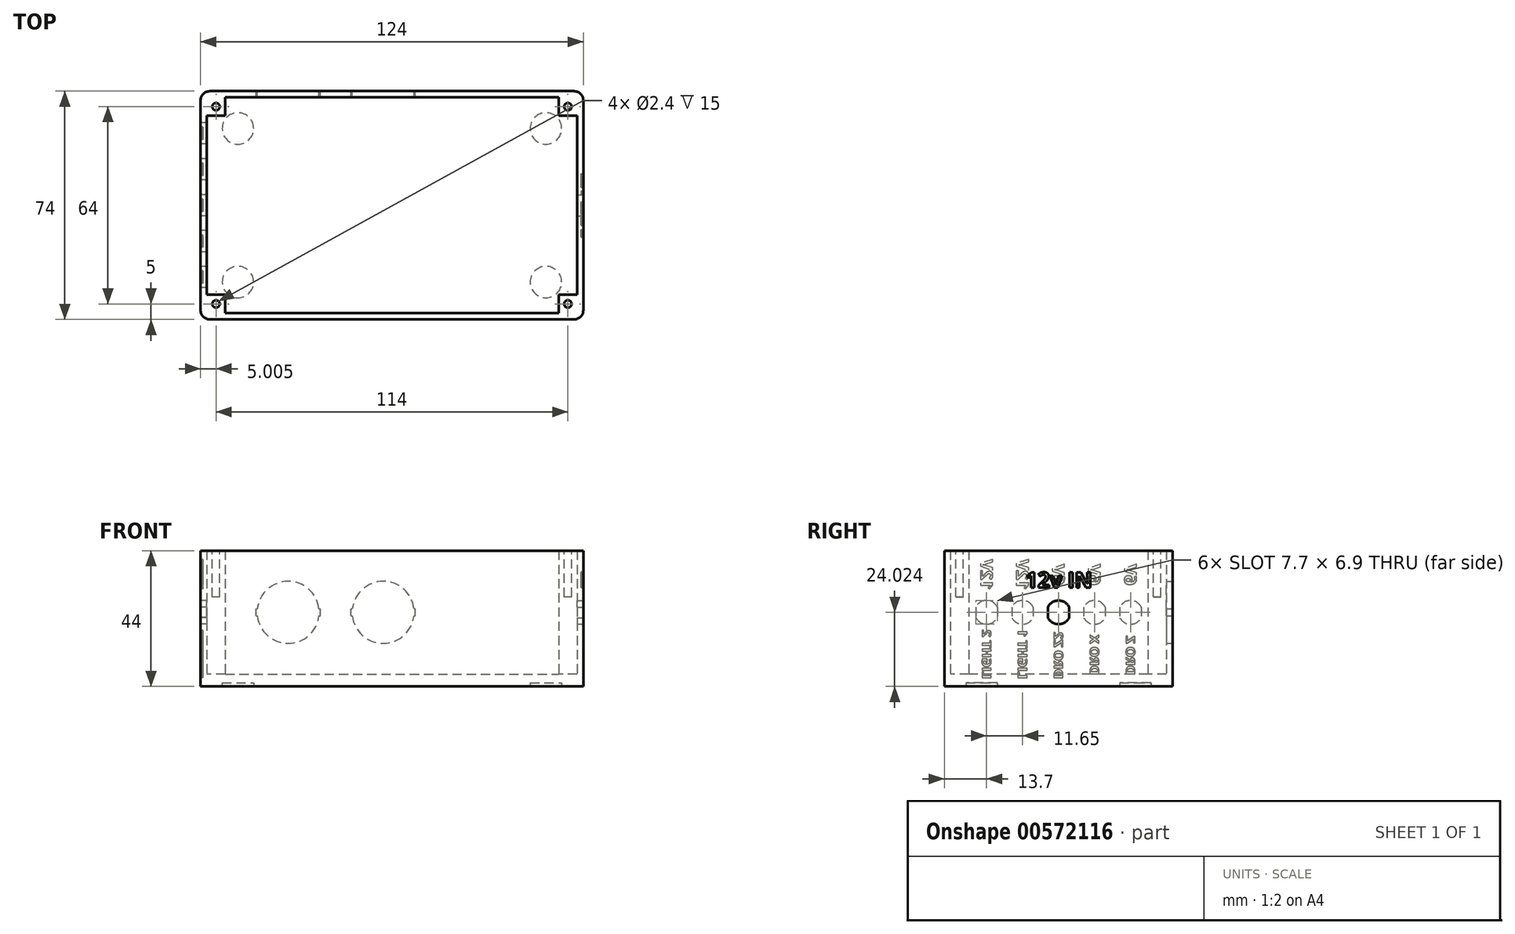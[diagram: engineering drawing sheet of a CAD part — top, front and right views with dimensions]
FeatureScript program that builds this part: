
annotation { "Feature Type Name" : "Feature", "Feature Type Description" : "" }
export const myFeature = defineFeature(function(context is Context, id is Id, definition is map)
    precondition{}
    {
        {
            var Q0;
            Q0=qCreatedBy(makeId("Top.planeOp"),FACE);
            var sketch = newSketch(context, id + "F0", { "sketchPlane" : qUnion([Q0])});
            skLineSegment(sketch, "E0.bottom", {"start": v(-65.67, 30.67) * mm, "end": v(58.33, 30.67) * mm});
            skLineSegment(sketch, "E0.top", {"start": v(-65.67, -43.33) * mm, "end": v(58.33, -43.33) * mm});
            skLineSegment(sketch, "E0.left", {"start": v(-65.67, 30.67) * mm, "end": v(-65.67, -43.33) * mm});
            skLineSegment(sketch, "E0.right", {"start": v(58.33, 30.67) * mm, "end": v(58.33, -43.33) * mm});
            skSolve(sketch);
        }
        {
            var Q0;
            Q0=makeQuery(id+"F0.imprint","IMPRINT",FACE,{"disambiguationData":[TD([[makeQuery(id+"F0.imprint","IMPRINT",EDGE,{"derivedFrom":sQuery(id+"F0.wireOp",EDGE,"E0.bottom")}),-1.0]])]});
            extrude(context, id + "F1", {"entities" : qUnion([Q0]), "depth" : 44 * mm, "offsetDistance" : 25 * mm});
        }
        {
            var Q0;
            Q0=makeQuery(id+"F1.opExtrude","CAP_FACE",FACE,{"disambiguationData":[OSD([sQuery(id+"F0.wireOp",EDGE,"E0.bottom"),sQuery(id+"F0.wireOp",EDGE,"E0.top"),sQuery(id+"F0.wireOp",EDGE,"E0.left"),sQuery(id+"F0.wireOp",EDGE,"E0.right")])],"isStart":false});
            var sketch = newSketch(context, id + "F2", { "sketchPlane" : qUnion([Q0])});
            skLineSegment(sketch, "E1.bottom", {"start": v(-63.67, 28.67) * mm, "end": v(56.33, 28.67) * mm});
            skLineSegment(sketch, "E1.top", {"start": v(-63.67, -41.33) * mm, "end": v(56.33, -41.33) * mm});
            skLineSegment(sketch, "E1.left", {"start": v(-63.67, 28.67) * mm, "end": v(-63.67, -41.33) * mm});
            skLineSegment(sketch, "E1.right", {"start": v(56.33, 28.67) * mm, "end": v(56.33, -41.33) * mm});
            skSolve(sketch);
        }
        {
            var Q0;
            Q0 = qSketchRegion(id + "F2", true);
            extrude(context, id + "F3", {"entities" : qUnion([Q0]), "operationType" : NewBodyOperationType.REMOVE, "oppositeDirection" : true, "depth" : 40 * mm, "offsetDistance" : 25 * mm});
        }
        {
            var Q0;
            Q0=makeQuery(id+"F3.boolean.opBoolean","COPY",FACE,{"derivedFrom":makeQuery(id+"F3.opExtrude","CAP_FACE",FACE,{"disambiguationData":[OSD([sQuery(id+"F2.wireOp",EDGE,"E1.bottom"),sQuery(id+"F2.wireOp",EDGE,"E1.top"),sQuery(id+"F2.wireOp",EDGE,"E1.left"),sQuery(id+"F2.wireOp",EDGE,"E1.right")])],"isStart":false})});
            var sketch = newSketch(context, id + "F4", { "sketchPlane" : qUnion([Q0])});
            skLineSegment(sketch, "E2.bottom", {"start": v(-57.67, 28.67) * mm, "end": v(-63.67, 28.67) * mm});
            skLineSegment(sketch, "E2.top", {"start": v(-57.67, 22.67) * mm, "end": v(-63.67, 22.67) * mm});
            skLineSegment(sketch, "E2.left", {"start": v(-57.67, 28.67) * mm, "end": v(-57.67, 22.67) * mm});
            skLineSegment(sketch, "E2.right", {"start": v(-63.67, 28.67) * mm, "end": v(-63.67, 22.67) * mm});
            skLineSegment(sketch, "E3.bottom", {"start": v(-63.67, -35.33) * mm, "end": v(-57.67, -35.33) * mm});
            skLineSegment(sketch, "E3.top", {"start": v(-63.67, -41.33) * mm, "end": v(-57.67, -41.33) * mm});
            skLineSegment(sketch, "E3.left", {"start": v(-63.67, -35.33) * mm, "end": v(-63.67, -41.33) * mm});
            skLineSegment(sketch, "E3.right", {"start": v(-57.67, -35.33) * mm, "end": v(-57.67, -41.33) * mm});
            skLineSegment(sketch, "E4.bottom", {"start": v(50.33, 28.67) * mm, "end": v(56.33, 28.67) * mm});
            skLineSegment(sketch, "E4.top", {"start": v(50.33, 22.67) * mm, "end": v(56.33, 22.67) * mm});
            skLineSegment(sketch, "E4.left", {"start": v(50.33, 28.67) * mm, "end": v(50.33, 22.67) * mm});
            skLineSegment(sketch, "E4.right", {"start": v(56.33, 28.67) * mm, "end": v(56.33, 22.67) * mm});
            skLineSegment(sketch, "E5.bottom", {"start": v(56.33, -35.33) * mm, "end": v(50.33, -35.33) * mm});
            skLineSegment(sketch, "E5.top", {"start": v(56.33, -41.33) * mm, "end": v(50.33, -41.33) * mm});
            skLineSegment(sketch, "E5.left", {"start": v(56.33, -35.33) * mm, "end": v(56.33, -41.33) * mm});
            skLineSegment(sketch, "E5.right", {"start": v(50.33, -35.33) * mm, "end": v(50.33, -41.33) * mm});
            skSolve(sketch);
        }
        {
            var Q0;
            Q0=makeQuery(id+"F4.imprint","IMPRINT",FACE,{"disambiguationData":[TD([[makeQuery(id+"F4.imprint","IMPRINT",EDGE,{"derivedFrom":sQuery(id+"F4.wireOp",EDGE,"E2.bottom")}),-1.0]])]});
            var Q1;
            Q1=makeQuery(id+"F4.imprint","IMPRINT",FACE,{"disambiguationData":[TD([[makeQuery(id+"F4.imprint","IMPRINT",EDGE,{"derivedFrom":sQuery(id+"F4.wireOp",EDGE,"E3.bottom")}),-1.0]])]});
            var Q2;
            Q2=makeQuery(id+"F4.imprint","IMPRINT",FACE,{"disambiguationData":[TD([[makeQuery(id+"F4.imprint","IMPRINT",EDGE,{"derivedFrom":sQuery(id+"F4.wireOp",EDGE,"E5.bottom")}),1.0]])]});
            var Q3;
            Q3=makeQuery(id+"F4.imprint","IMPRINT",FACE,{"disambiguationData":[TD([[makeQuery(id+"F4.imprint","IMPRINT",EDGE,{"derivedFrom":sQuery(id+"F4.wireOp",EDGE,"E4.bottom")}),-1.0]])]});
            extrude(context, id + "F5", {"entities" : qUnion([Q0, Q1, Q2, Q3]), "operationType" : NewBodyOperationType.ADD, "depth" : 40 * mm, "offsetDistance" : 25 * mm});
        }
        {
            var Q0;
            Q0=makeQuery(id+"F1.opExtrude","SWEPT_FACE",FACE,{"disambiguationData":[OSD([sQuery(id+"F0.wireOp",EDGE,"E0.right")])]});
            var sketch = newSketch(context, id + "F6", { "sketchPlane" : qUnion([Q0])});
            skPoint(sketch, "E6.centerSnap0", {"position": v(-43.33, 22) * mm});
            skPoint(sketch, "E6.centerSnap1", {"position": v(-6.33, 44) * mm});
            skText(sketch, "E7", { "text": "12v IN", "fontName": "OpenSans-Bold.ttf"});
            skLineSegment(sketch, "E8", {"start": v(-6.33, 44) * mm, "end": v(-6.33, 0) * mm, "construction": true});
            skLineSegment(sketch, "E9", {"start": v(-46.35, 24) * mm, "end": v(35.36, 24) * mm, "construction": true});
            skLineSegment(sketch, "E10", {"start": v(-47, 4) * mm, "end": v(35.52, 4) * mm, "construction": true});
            const initialGuessF6  = {"E7": [-0.01706, 0.03203, 1, 0, 0.005]};
            skSetInitialGuess(sketch, initialGuessF6);
            skSolve(sketch);
        }
        {
            var Q0;
            Q0 = qSketchRegion(id + "F6", true);
            extrude(context, id + "F7", {"entities" : qUnion([Q0]), "operationType" : NewBodyOperationType.REMOVE, "oppositeDirection" : true, "depth" : 0.7 * mm, "offsetDistance" : 25 * mm});
        }
        {
            var Q0;
            Q0=makeQuery(id+"F6.imprint","IMPRINT",FACE,{"disambiguationData":[TD([[makeQuery(id+"F6.imprint","IMPRINT",EDGE,{"derivedFrom":sQuery(id+"F6.wireOp",EDGE,"E7.sketch_text.stroke-0")}),1.0]])]});
            var sketch = newSketch(context, id + "F8", { "sketchPlane" : qUnion([Q0])});
            skLineSegment(sketch, "E11", {"start": v(33.2, 0) * mm, "end": v(-45.85, 0) * mm, "construction": true});
            skLineSegment(sketch, "E12", {"start": v(-45.85, 4) * mm, "end": v(34.48, 4) * mm, "construction": true});
            skLineSegment(sketch, "E13", {"start": v(34.48, 24) * mm, "end": v(-45.85, 24) * mm, "construction": true});
            skLineSegment(sketch, "E14", {"start": v(30.67, 0) * mm, "end": v(30.67, 44.64) * mm, "construction": true});
            skLineSegment(sketch, "E15", {"start": v(-43.33, 0) * mm, "end": v(-43.33, 45.27) * mm, "construction": true});
            skLineSegment(sketch, "E16", {"start": v(-6.33, -5.83) * mm, "end": v(-6.33, 47.57) * mm, "construction": true});
            skPoint(sketch, "E16.startSnap0", {"position": v(-6.33, 0) * mm});
            skArc(sketch, "E17", {"start": v(-9.78, 22.3) * mm, "mid": v(-6.33, 20.15) * mm, "end": v(-2.88, 22.3) * mm});
            skLineSegment(sketch, "E18", {"start": v(-2.88, 25.7) * mm, "end": v(-2.88, 22.3) * mm});
            skLineSegment(sketch, "E19", {"start": v(-9.78, 25.7) * mm, "end": v(-9.78, 22.3) * mm});
            skArc(sketch, "E20.trimOffspring", {"start": v(-2.88, 25.7) * mm, "mid": v(-6.33, 27.85) * mm, "end": v(-9.78, 25.7) * mm});
            skSolve(sketch);
        }
        {
            var Q0;
            Q0=makeQuery(id+"F1.opExtrude","CAP_FACE",FACE,{"disambiguationData":[OSD([sQuery(id+"F0.wireOp",EDGE,"E0.bottom"),sQuery(id+"F0.wireOp",EDGE,"E0.top"),sQuery(id+"F0.wireOp",EDGE,"E0.left"),sQuery(id+"F0.wireOp",EDGE,"E0.right")])],"isStart":true});
            var sketch = newSketch(context, id + "F9", { "sketchPlane" : qUnion([Q0])});
            skCircle(sketch, "E21", {"center": v(46.23, 31.23) * mm, "radius": 5.1 * mm});
            skCircle(sketch, "E22", {"center": v(46.23, -18.57) * mm, "radius": 5.1 * mm});
            skCircle(sketch, "E23", {"center": v(-53.57, 31.23) * mm, "radius": 5.1 * mm});
            skCircle(sketch, "E24", {"center": v(-53.57, -18.57) * mm, "radius": 5.1 * mm});
            skSolve(sketch);
        }
        {
            var Q0;
            Q0=makeQuery(id+"F9.imprint","IMPRINT",FACE,{"disambiguationData":[TD([[makeQuery(id+"F9.imprint","IMPRINT",EDGE,{"derivedFrom":sQuery(id+"F9.wireOp",EDGE,"E23")}),1.0]])]});
            var Q1;
            Q1=makeQuery(id+"F9.imprint","IMPRINT",FACE,{"disambiguationData":[TD([[makeQuery(id+"F9.imprint","IMPRINT",EDGE,{"derivedFrom":sQuery(id+"F9.wireOp",EDGE,"E24")}),1.0]])]});
            var Q2;
            Q2=makeQuery(id+"F9.imprint","IMPRINT",FACE,{"disambiguationData":[TD([[makeQuery(id+"F9.imprint","IMPRINT",EDGE,{"derivedFrom":sQuery(id+"F9.wireOp",EDGE,"E22")}),1.0]])]});
            var Q3;
            Q3=makeQuery(id+"F9.imprint","IMPRINT",FACE,{"disambiguationData":[TD([[makeQuery(id+"F9.imprint","IMPRINT",EDGE,{"derivedFrom":sQuery(id+"F9.wireOp",EDGE,"E21")}),1.0]])]});
            extrude(context, id + "F10", {"entities" : qUnion([Q0, Q1, Q2, Q3]), "operationType" : NewBodyOperationType.REMOVE, "oppositeDirection" : true, "depth" : 1.1 * mm, "offsetDistance" : 25 * mm});
        }
        {
            var Q0;
            Q0=makeQuery(id+"F5.boolean.opBoolean","MERGE",FACE,{"derivedFrom":[makeQuery(id+"F1.opExtrude","CAP_FACE",FACE,{"disambiguationData":[OSD([sQuery(id+"F0.wireOp",EDGE,"E0.bottom"),sQuery(id+"F0.wireOp",EDGE,"E0.top"),sQuery(id+"F0.wireOp",EDGE,"E0.left"),sQuery(id+"F0.wireOp",EDGE,"E0.right")])],"isStart":false}),makeQuery(id+"F5.opExtrude","CAP_FACE",FACE,{"disambiguationData":[OSD([sQuery(id+"F4.wireOp",EDGE,"E2.bottom"),sQuery(id+"F4.wireOp",EDGE,"E2.top"),sQuery(id+"F4.wireOp",EDGE,"E2.left"),sQuery(id+"F4.wireOp",EDGE,"E2.right")])],"isStart":false}),makeQuery(id+"F5.opExtrude","CAP_FACE",FACE,{"disambiguationData":[OSD([sQuery(id+"F4.wireOp",EDGE,"E3.bottom"),sQuery(id+"F4.wireOp",EDGE,"E3.top"),sQuery(id+"F4.wireOp",EDGE,"E3.left"),sQuery(id+"F4.wireOp",EDGE,"E3.right")])],"isStart":false}),makeQuery(id+"F5.opExtrude","CAP_FACE",FACE,{"disambiguationData":[OSD([sQuery(id+"F4.wireOp",EDGE,"E4.bottom"),sQuery(id+"F4.wireOp",EDGE,"E4.top"),sQuery(id+"F4.wireOp",EDGE,"E4.left"),sQuery(id+"F4.wireOp",EDGE,"E4.right")])],"isStart":false}),makeQuery(id+"F5.opExtrude","CAP_FACE",FACE,{"disambiguationData":[OSD([sQuery(id+"F4.wireOp",EDGE,"E5.bottom"),sQuery(id+"F4.wireOp",EDGE,"E5.top"),sQuery(id+"F4.wireOp",EDGE,"E5.left"),sQuery(id+"F4.wireOp",EDGE,"E5.right")])],"isStart":false})]});
            var sketch = newSketch(context, id + "F11", { "sketchPlane" : qUnion([Q0])});
            skCircle(sketch, "E25", {"center": v(-60.67, 25.67) * mm, "radius": 1.2 * mm});
            skPoint(sketch, "E25.centerSnap0", {"position": v(-60.67, 22.67) * mm});
            skPoint(sketch, "E25.centerSnap1", {"position": v(-57.67, 25.67) * mm});
            skCircle(sketch, "E26", {"center": v(-60.67, -38.33) * mm, "radius": 1.2 * mm});
            skPoint(sketch, "E26.centerSnap0", {"position": v(-60.67, -35.33) * mm});
            skPoint(sketch, "E26.centerSnap1", {"position": v(-57.67, -38.33) * mm});
            skCircle(sketch, "E27", {"center": v(53.33, 25.67) * mm, "radius": 1.2 * mm});
            skPoint(sketch, "E27.centerSnap0", {"position": v(50.33, 25.67) * mm});
            skPoint(sketch, "E27.centerSnap1", {"position": v(53.33, 22.67) * mm});
            skCircle(sketch, "E28", {"center": v(53.33, -38.33) * mm, "radius": 1.2 * mm});
            skPoint(sketch, "E28.centerSnap0", {"position": v(50.33, -38.33) * mm});
            skPoint(sketch, "E28.centerSnap1", {"position": v(53.33, -35.33) * mm});
            skSolve(sketch);
        }
        {
            var Q0;
            Q0=makeQuery(id+"F11.imprint","IMPRINT",FACE,{"disambiguationData":[TD([[makeQuery(id+"F11.imprint","IMPRINT",EDGE,{"derivedFrom":sQuery(id+"F11.wireOp",EDGE,"E26")}),1.0]])]});
            var Q1;
            Q1=makeQuery(id+"F11.imprint","IMPRINT",FACE,{"disambiguationData":[TD([[makeQuery(id+"F11.imprint","IMPRINT",EDGE,{"derivedFrom":sQuery(id+"F11.wireOp",EDGE,"E27")}),1.0]])]});
            var Q2;
            Q2=makeQuery(id+"F11.imprint","IMPRINT",FACE,{"disambiguationData":[TD([[makeQuery(id+"F11.imprint","IMPRINT",EDGE,{"derivedFrom":sQuery(id+"F11.wireOp",EDGE,"E28")}),1.0]])]});
            var Q3;
            Q3=makeQuery(id+"F11.imprint","IMPRINT",FACE,{"disambiguationData":[TD([[makeQuery(id+"F11.imprint","IMPRINT",EDGE,{"derivedFrom":sQuery(id+"F11.wireOp",EDGE,"E25")}),1.0]])]});
            extrude(context, id + "F12", {"entities" : qUnion([Q0, Q1, Q2, Q3]), "operationType" : NewBodyOperationType.REMOVE, "oppositeDirection" : true, "depth" : 15 * mm, "offsetDistance" : 25 * mm});
        }
        {
            var Q0;
            Q0=makeQuery(id+"F1.opExtrude","SWEPT_FACE",FACE,{"disambiguationData":[OSD([sQuery(id+"F0.wireOp",EDGE,"E0.bottom")])]});
            var sketch = newSketch(context, id + "F13", { "sketchPlane" : qUnion([Q0])});
            skArc(sketch, "E29", {"start": v(27.3, 22.85) * mm, "mid": v(37.28, 13.95) * mm, "end": v(47.26, 22.85) * mm});
            skLineSegment(sketch, "E30.bottom", {"start": v(47.67, 22.85) * mm, "end": v(47.26, 22.85) * mm});
            skLineSegment(sketch, "E30.top", {"start": v(47.67, 25.15) * mm, "end": v(47.26, 25.15) * mm});
            skLineSegment(sketch, "E30.left", {"start": v(47.67, 22.85) * mm, "end": v(47.67, 25.15) * mm});
            skLineSegment(sketch, "E30.right", {"start": v(26.9, 22.85) * mm, "end": v(26.9, 25.15) * mm});
            skLineSegment(sketch, "E31.trimOffspring", {"start": v(27.3, 22.85) * mm, "end": v(26.9, 22.85) * mm});
            skArc(sketch, "E32.trimOffspring", {"start": v(47.26, 25.15) * mm, "mid": v(37.28, 34.05) * mm, "end": v(27.3, 25.15) * mm});
            skLineSegment(sketch, "E33.trimOffspring", {"start": v(27.3, 25.15) * mm, "end": v(26.9, 25.15) * mm});
            skLineSegment(sketch, "E34", {"start": v(37.28, 24) * mm, "end": v(-29.07, 24) * mm, "construction": true});
            skLineSegment(sketch, "E35", {"start": v(37.28, 24) * mm, "end": v(65.67, 24) * mm, "construction": true});
            skLineSegment(sketch, "E36", {"start": v(57.67, 44) * mm, "end": v(57.67, 0) * mm, "construction": true});
            skLineSegment(sketch, "E37", {"start": v(1.3, 4) * mm, "end": v(75.25, 4) * mm, "construction": true});
            skArc(sketch, "E38", {"start": v(-3.48, 22.85) * mm, "mid": v(6.5, 13.95) * mm, "end": v(16.49, 22.85) * mm});
            skLineSegment(sketch, "E39.bottom", {"start": v(16.9, 22.85) * mm, "end": v(16.49, 22.85) * mm});
            skLineSegment(sketch, "E39.top", {"start": v(16.9, 25.15) * mm, "end": v(16.49, 25.15) * mm});
            skLineSegment(sketch, "E39.left", {"start": v(16.9, 22.85) * mm, "end": v(16.9, 25.15) * mm});
            skLineSegment(sketch, "E39.right", {"start": v(-3.88, 22.85) * mm, "end": v(-3.88, 25.15) * mm});
            skLineSegment(sketch, "E40.trimOffspring", {"start": v(-3.48, 22.85) * mm, "end": v(-3.88, 22.85) * mm});
            skArc(sketch, "E41.trimOffspring", {"start": v(16.49, 25.15) * mm, "mid": v(6.5, 34.05) * mm, "end": v(-3.48, 25.15) * mm});
            skLineSegment(sketch, "E42.trimOffspring", {"start": v(-3.48, 25.15) * mm, "end": v(-3.88, 25.15) * mm});
            skSolve(sketch);
        }
        {
            var Q0;
            Q0=makeQuery(id+"F13.imprint","IMPRINT",FACE,{"disambiguationData":[TD([[makeQuery(id+"F13.imprint","IMPRINT",EDGE,{"derivedFrom":sQuery(id+"F13.wireOp",EDGE,"E29")}),1.0]])]});
            var Q1;
            Q1=makeQuery(id+"F13.imprint","IMPRINT",FACE,{"disambiguationData":[TD([[makeQuery(id+"F13.imprint","IMPRINT",EDGE,{"derivedFrom":sQuery(id+"F13.wireOp",EDGE,"E38")}),1.0]])]});
            extrude(context, id + "F14", {"entities" : qUnion([Q0, Q1]), "operationType" : NewBodyOperationType.REMOVE, "endBound" : BoundingType.UP_TO_NEXT, "oppositeDirection" : true, "depth" : 3 * mm, "offsetDistance" : 25 * mm});
        }
        {
            var Q0;
            Q0=makeQuery(id+"F1.opExtrude","SWEPT_FACE",FACE,{"disambiguationData":[OSD([sQuery(id+"F0.wireOp",EDGE,"E0.left")])]});
            var sketch = newSketch(context, id + "F15", { "sketchPlane" : qUnion([Q0])});
            skLineSegment(sketch, "E43", {"start": v(-47.32, 4) * mm, "end": v(59.37, 4) * mm, "construction": true});
            skLineSegment(sketch, "E44", {"start": v(-24.67, 44) * mm, "end": v(-24.67, 0) * mm, "construction": true});
            skLineSegment(sketch, "E45", {"start": v(37.33, 44) * mm, "end": v(37.33, 0) * mm, "construction": true});
            skPoint(sketch, "E46.startSnap0", {"position": v(6.33, 44) * mm});
            skPoint(sketch, "E46.endSnap0", {"position": v(6.33, 0) * mm});
            skArc(sketch, "E47", {"start": v(2.88, 22.3) * mm, "mid": v(6.33, 20.15) * mm, "end": v(9.78, 22.3) * mm});
            skArc(sketch, "E48", {"start": v(26.18, 22.32) * mm, "mid": v(29.63, 20.17) * mm, "end": v(33.08, 22.32) * mm});
            skLineSegment(sketch, "E49", {"start": v(6.33, 44) * mm, "end": v(6.33, 0) * mm, "construction": true});
            skArc(sketch, "E50", {"start": v(14.53, 22.3) * mm, "mid": v(17.98, 20.15) * mm, "end": v(21.43, 22.3) * mm});
            skArc(sketch, "E51", {"start": v(-8.77, 22.3) * mm, "mid": v(-5.32, 20.15) * mm, "end": v(-1.87, 22.3) * mm});
            skArc(sketch, "E52", {"start": v(-13.55, 25.7) * mm, "mid": v(-17, 27.85) * mm, "end": v(-20.45, 25.7) * mm});
            skPoint(sketch, "E53", {"position": v(23.15, 24) * mm});
            skLineSegment(sketch, "E54", {"start": v(-33.7, 24) * mm, "end": v(49.69, 24) * mm, "construction": true});
            skLineSegment(sketch, "E55", {"start": v(33.48, 35.36) * mm, "end": v(33.48, 8.32) * mm, "construction": true});
            skLineSegment(sketch, "E56", {"start": v(-13.55, 25.7) * mm, "end": v(-13.55, 22.3) * mm});
            skLineSegment(sketch, "E57", {"start": v(-20.45, 25.7) * mm, "end": v(-20.45, 22.3) * mm});
            skLineSegment(sketch, "E58", {"start": v(-8.77, 25.7) * mm, "end": v(-8.77, 22.3) * mm});
            skLineSegment(sketch, "E59", {"start": v(-1.87, 25.7) * mm, "end": v(-1.87, 22.3) * mm});
            skLineSegment(sketch, "E60", {"start": v(2.88, 25.7) * mm, "end": v(2.88, 22.3) * mm});
            skLineSegment(sketch, "E61", {"start": v(9.78, 25.7) * mm, "end": v(9.78, 22.3) * mm});
            skLineSegment(sketch, "E62", {"start": v(14.53, 25.7) * mm, "end": v(14.53, 22.3) * mm});
            skLineSegment(sketch, "E63", {"start": v(21.43, 25.7) * mm, "end": v(21.43, 22.3) * mm});
            skLineSegment(sketch, "E64", {"start": v(26.18, 25.73) * mm, "end": v(26.18, 22.32) * mm});
            skLineSegment(sketch, "E65", {"start": v(33.08, 25.73) * mm, "end": v(33.08, 22.32) * mm});
            skArc(sketch, "E66.trimOffspring", {"start": v(-20.45, 22.3) * mm, "mid": v(-17, 20.15) * mm, "end": v(-13.55, 22.3) * mm});
            skArc(sketch, "E67.trimOffspring", {"start": v(-1.87, 25.7) * mm, "mid": v(-5.32, 27.85) * mm, "end": v(-8.77, 25.7) * mm});
            skArc(sketch, "E68.trimOffspring", {"start": v(9.78, 25.7) * mm, "mid": v(6.33, 27.85) * mm, "end": v(2.88, 25.7) * mm});
            skArc(sketch, "E69.trimOffspring", {"start": v(21.43, 25.7) * mm, "mid": v(17.98, 27.85) * mm, "end": v(14.53, 25.7) * mm});
            skArc(sketch, "E70.trimOffspring", {"start": v(33.48, 24) * mm, "mid": v(33.48, 24.01) * mm, "end": v(33.48, 24.02) * mm});
            skArc(sketch, "E71.trimOffspring", {"start": v(33.08, 25.73) * mm, "mid": v(29.63, 27.87) * mm, "end": v(26.18, 25.73) * mm});
            skSolve(sketch);
        }
        {
            var Q0;
            Q0 = qSketchRegion(id + "F15", true);
            extrude(context, id + "F16", {"entities" : qUnion([Q0]), "operationType" : NewBodyOperationType.REMOVE, "endBound" : BoundingType.UP_TO_NEXT, "oppositeDirection" : true, "depth" : 25 * mm, "offsetDistance" : 25 * mm});
        }
        {
            var Q0;
            Q0=makeQuery(id+"F1.opExtrude","SWEPT_EDGE",EDGE,{"disambiguationData":[OSD([sQuery(id+"F0.wireOp",EDGE,"E0.top"),sQuery(id+"F0.wireOp",EDGE,"E0.left")])]});
            var Q1;
            Q1=makeQuery(id+"F1.opExtrude","SWEPT_EDGE",EDGE,{"disambiguationData":[OSD([sQuery(id+"F0.wireOp",EDGE,"E0.top"),sQuery(id+"F0.wireOp",EDGE,"E0.right")])]});
            var Q2;
            Q2=makeQuery(id+"F1.opExtrude","SWEPT_EDGE",EDGE,{"disambiguationData":[OSD([sQuery(id+"F0.wireOp",EDGE,"E0.bottom"),sQuery(id+"F0.wireOp",EDGE,"E0.right")])]});
            var Q3;
            Q3=makeQuery(id+"F1.opExtrude","SWEPT_EDGE",EDGE,{"disambiguationData":[OSD([sQuery(id+"F0.wireOp",EDGE,"E0.bottom"),sQuery(id+"F0.wireOp",EDGE,"E0.left")])]});
            fillet(context, id + "F17", {"entities" : qUnion([Q0, Q1, Q2, Q3]), "radius" : 3 * mm, "tangentPropagation" : true, "allowEdgeOverflow" : false});
        }
        {
            var Q0;
            Q0 = qSketchRegion(id + "F8", true);
            extrude(context, id + "F18", {"entities" : qUnion([Q0]), "operationType" : NewBodyOperationType.REMOVE, "endBound" : BoundingType.UP_TO_NEXT, "oppositeDirection" : true, "depth" : 25 * mm, "offsetDistance" : 25 * mm});
        }
        {
            var Q0;
            Q0=makeQuery(id+"F1.opExtrude","SWEPT_FACE",FACE,{"disambiguationData":[OSD([sQuery(id+"F0.wireOp",EDGE,"E0.left")])]});
            var sketch = newSketch(context, id + "F19", { "sketchPlane" : qUnion([Q0])});
            skLineSegment(sketch, "E72", {"start": v(-39.65, 32.86) * mm, "end": v(32.9, 32.86) * mm, "construction": true});
            skLineSegment(sketch, "E73", {"start": v(-39.65, 40) * mm, "end": v(32.9, 40) * mm, "construction": true});
            skLineSegment(sketch, "E74", {"start": v(-17, 24) * mm, "end": v(-17, 0) * mm, "construction": true});
            skLineSegment(sketch, "E75", {"start": v(-5.32, 24) * mm, "end": v(-5.32, 0) * mm, "construction": true});
            skLineSegment(sketch, "E76", {"start": v(6.33, 24) * mm, "end": v(6.33, 0) * mm, "construction": true});
            skLineSegment(sketch, "E77", {"start": v(17.98, 40) * mm, "end": v(17.98, 0) * mm, "construction": true});
            skLineSegment(sketch, "E78", {"start": v(29.63, 40) * mm, "end": v(29.63, 0) * mm, "construction": true});
            skLineSegment(sketch, "E79", {"start": v(-17, 24) * mm, "end": v(-17, 44) * mm, "construction": true});
            skLineSegment(sketch, "E80", {"start": v(-5.32, 24) * mm, "end": v(-5.32, 44) * mm, "construction": true});
            skLineSegment(sketch, "E81", {"start": v(6.33, 24) * mm, "end": v(6.33, 44) * mm, "construction": true});
            skLineSegment(sketch, "E82.trimOffspring", {"start": v(-22.33, 40) * mm, "end": v(-22.33, 44) * mm, "construction": true});
            skText(sketch, "E83", { "text": "6V", "fontName": "OpenSans-Bold.ttf"});
            skText(sketch, "E84", { "text": "DRO Z", "fontName": "OpenSans-Bold.ttf"});
            skText(sketch, "E85", { "text": "DRO X", "fontName": "OpenSans-Bold.ttf"});
            skText(sketch, "E86", { "text": "6V", "fontName": "OpenSans-Bold.ttf"});
            skText(sketch, "E87", { "text": "DRO Z2", "fontName": "OpenSans-Bold.ttf"});
            skText(sketch, "E88", { "text": "6V", "fontName": "OpenSans-Bold.ttf"});
            skText(sketch, "E89", { "text": "LIGHT 1", "fontName": "OpenSans-Bold.ttf"});
            skText(sketch, "E90", { "text": "LIGHT 2", "fontName": "OpenSans-Bold.ttf"});
            skText(sketch, "E91", { "text": "12V", "fontName": "OpenSans-Bold.ttf"});
            skText(sketch, "E92", { "text": "12V", "fontName": "OpenSans-Bold.ttf"});
            skPoint(sketch, "E93.orphan", {"position": v(29.63, 24.02) * mm});
            skPoint(sketch, "E94.orphan", {"position": v(17.98, 24) * mm});
            skLineSegment(sketch, "E95", {"start": v(-27.67, 0) * mm, "end": v(40.33, 0) * mm, "construction": true});
            const initialGuessF19  = {"E83": [-0.015, 0.03286, 0, 1, 0.004], "E84": [-0.0155, 0.00368, 0, 1, 0.003], "E85": [-0.00382, 0.00369, 0, 1, 0.003], "E86": [-0.00332, 0.03286, 0, 1, 0.004], "E87": [0.00783, 0.0025, 0, 1, 0.003], "E88": [0.00833, 0.03286, 0, 1, 0.004], "E89": [0.01948, 0.0025, 0, 1, 0.003], "E90": [0.03113, 0.0025, 0, 1, 0.003], "E91": [0.01998, 0.03127, 0, 1, 0.004], "E92": [0.03163, 0.03127, 0, 1, 0.004]};
            skSetInitialGuess(sketch, initialGuessF19);
            skSolve(sketch);
        }
        {
            var Q0;
            Q0 = qSketchRegion(id + "F19", true);
            extrude(context, id + "F20", {"entities" : qUnion([Q0]), "operationType" : NewBodyOperationType.REMOVE, "oppositeDirection" : true, "depth" : 0.75 * mm, "offsetDistance" : 25 * mm});
        }
    });
